# Revit family: Typ.B_TP&N_250A_Side_Extension_Boxes-empty-NoHosted-UK-en
name_source: partatom
category: Electrical Equipment
units: mm (PartAtom-declared; Revit-internal decimal feet)

## family parameters
Always vertical = Yes
Cut with Voids When Loaded = No
Panel Configuration = Two Columns, Circuits Across
Part Type = Panelboard
Room Calculation Point = No
Round Connector Dimension = Use Diameter
Shared = No
Work Plane-Based = Yes

## types (5) — shared parameters
Default Elevation = 1219 mm
EF000003 - Mounting method = EV000384 - Surface mounted (plaster)
EF000008 - Width = 465 mm  [stored 1.52559 ft]
EF000118 - With mounting plate = No
EF000339 - Type of cover = EV004216 - Door
EF001062 - EMC-version = No
EF001088 - Extension possible = No
EF001134 - DIN-rail = No
EF006244 - Transparent cover/door = No
EF006306 - With lock = No
EF015776 - Earthing terminal block = No
EF015777 - Neutral terminal block = No
EF015941 - Signal passing door = No
HG000002 - With door or cover = Yes
HG000003 - Range = Type B TP&N Distribution Boards
HG000005 - Thickness = 3 mm  [stored 0.00984252 ft]
HG000006 - Flush mounted = No
HG000009 - Double swing door = No
HG000010 - Asymmetric doors = No
HG000011 - Empty rows from bottom = No
HG000017 - Distance between poles = 18 mm  [stored 0.0590551 ft]
Manufacturer = Hager
Type Comments = Type B TP&N Distribution Boards
zero-valued in all types: EF000218 - Built-in depth, EF000266 - Number of rows, EF000332 - Built-in height, EF000846 - Built-in width, EF001131 - Internal depth, EF002950 - Width in number of modular spacings, HG000001 - Number of columns, HG000007 - Number of empty columns, HG000008 - Number of empty rows

## per-type parameters (varying)
| type | EF000007 - Colour | EF000040 - Height | EF000049 - Depth | EF000116 - RAL-number | EF001596 - Material housing | EF004462 - Type of closure | EF005474 - Degree of protection (IP) | HG000004 - Manufacturer reference | Model |
| Surface mounted  W465 H1100 D165.5 0 Modular spacings - JK212BSF |  | 1100 mm | 166 mm |  |  |  |  | JK212BSF | JK212BSF |
| Surface mounted  W465 H1250 D165.5 0 Modular spacings - JK216BSF |  | 1250 mm  [stored 4.10105 ft] | 166 mm |  |  |  |  | JK216BSF | JK216BSF |
| Surface mounted  W465 H1400 D165.5 0 Modular spacings - JK218BSF |  | 1400 mm | 166 mm |  |  |  |  | JK218BSF | JK218BSF |
| Surface mounted P2XC W465 H1550 D165.5 0 Modular spacings - JK224BSF | EV000154 - Other | 1550 mm | 166 mm | 7035 | EV000179 - Steel | EV000154 - Other | EV009848 - IP2XC | JK224BSF | JK224BSF |
| Surface mounted P2XC W465 H950 D124.5 0 Modular spacings - JK208BSF | EV000154 - Other | 950 mm  [stored 3.1168 ft] | 124 mm  [stored 0.406824 ft] | 7035 | EV000179 - Steel | EV000154 - Other | EV009848 - IP2XC | JK208BSF | JK208BSF |

note: [stored X ft] marks values corroborated as IEEE doubles in the binary element streams (Revit-internal decimal feet)

## geometry (parser evidence)
native form markers: Sweep x14
no freeform markers — native parametric forms only
